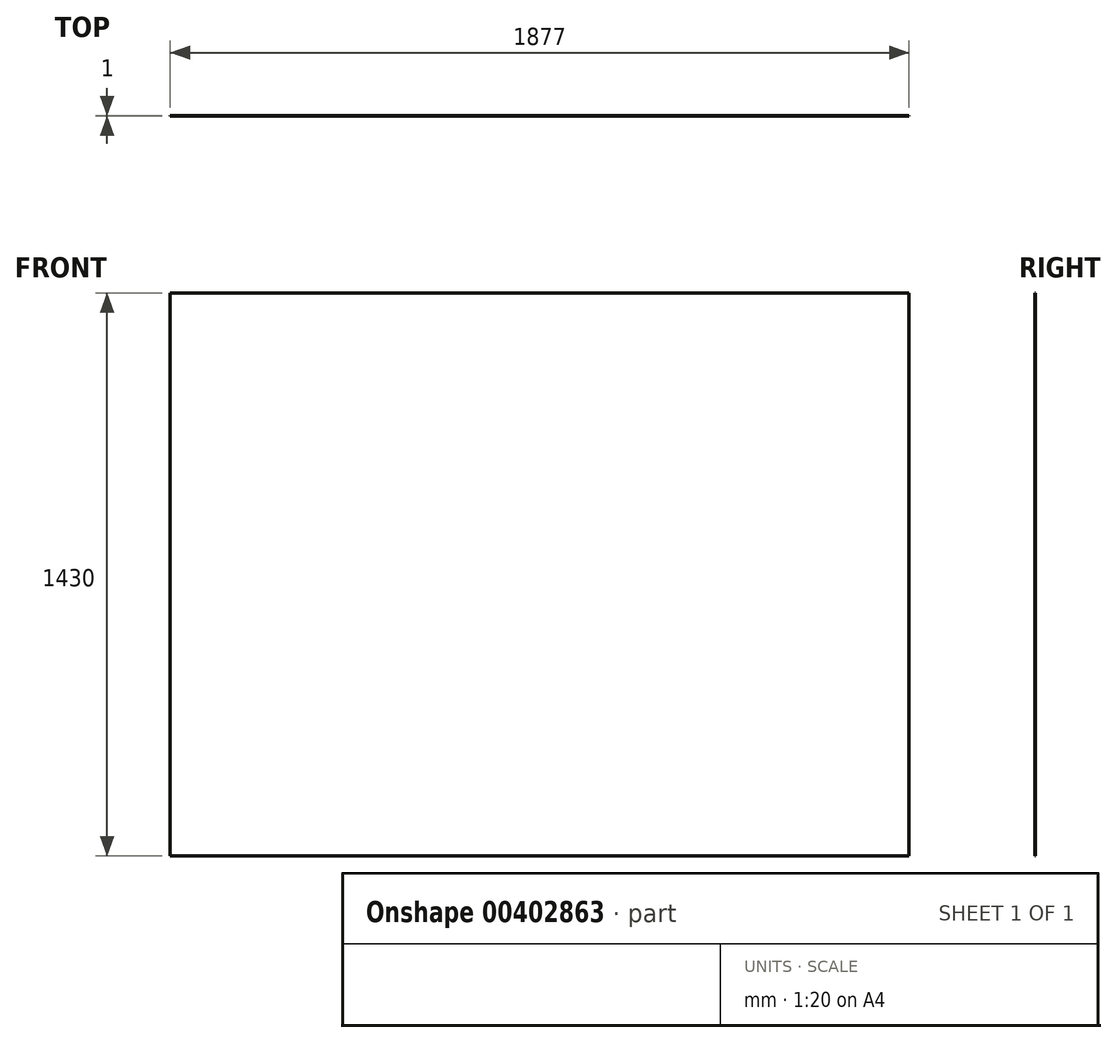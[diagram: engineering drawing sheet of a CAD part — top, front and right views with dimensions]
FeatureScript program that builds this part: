
annotation { "Feature Type Name" : "Feature", "Feature Type Description" : "" }
export const myFeature = defineFeature(function(context is Context, id is Id, definition is map)
    precondition{}
    {
        {
            var Q0;
            Q0=qCreatedBy(makeId("Front.planeOp"),FACE);
            var sketch = newSketch(context, id + "F0", { "sketchPlane" : qUnion([Q0])});
            skLineSegment(sketch, "E0.bottom", {"start": v(-938.5, 715) * mm, "end": v(938.5, 715) * mm});
            skLineSegment(sketch, "E0.top", {"start": v(-938.5, -715) * mm, "end": v(938.5, -715) * mm});
            skLineSegment(sketch, "E0.left", {"start": v(-938.5, 715) * mm, "end": v(-938.5, -715) * mm});
            skLineSegment(sketch, "E0.right", {"start": v(938.5, 715) * mm, "end": v(938.5, -715) * mm});
            skPoint(sketch, "E0.middle", {"position": v(0, 0) * mm});
            skSolve(sketch);
        }
        {
            var Q0;
            Q0=makeQuery(id+"F0.imprint","IMPRINT",FACE,{"disambiguationData":[TD([[makeQuery(id+"F0.imprint","IMPRINT",EDGE,{"derivedFrom":sQuery(id+"F0.wireOp",EDGE,"E0.bottom")}),-1.0]])]});
            extrude(context, id + "F1", {"entities" : qUnion([Q0]), "depth" : 1 * mm});
        }
    });
